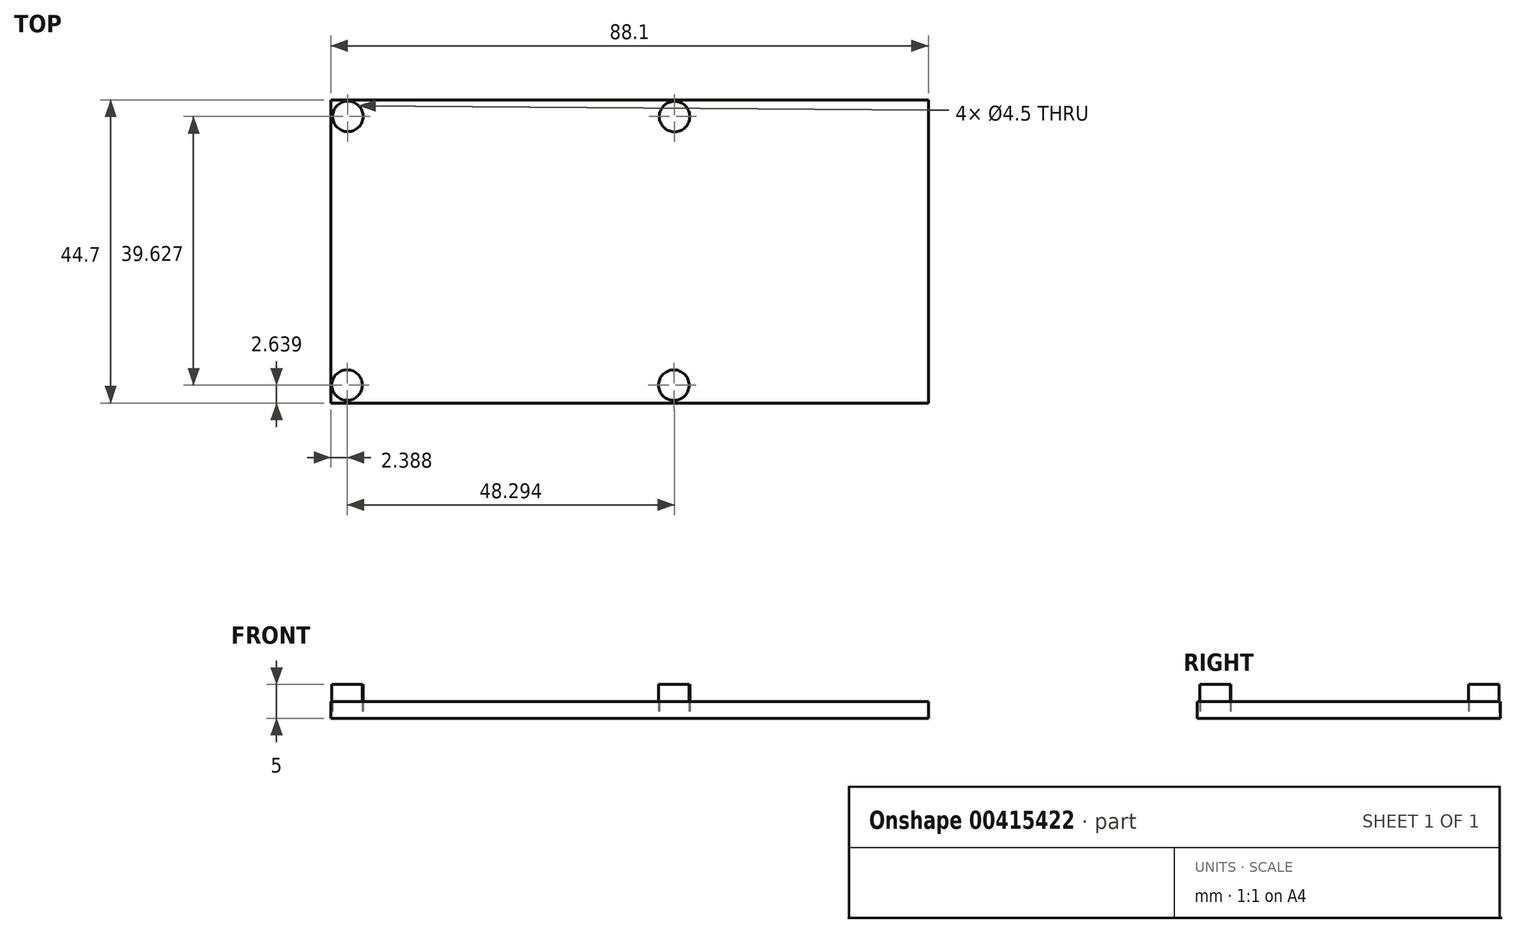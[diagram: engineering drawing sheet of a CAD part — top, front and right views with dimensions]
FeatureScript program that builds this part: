
annotation { "Feature Type Name" : "Feature", "Feature Type Description" : "" }
export const myFeature = defineFeature(function(context is Context, id is Id, definition is map)
    precondition{}
    {
        {
            var Q0;
            Q0=qCreatedBy(makeId("Top.planeOp"),FACE);
            var sketch = newSketch(context, id + "F0", { "sketchPlane" : qUnion([Q0])});
            skLineSegment(sketch, "E0.bottom", {"start": v(26.55, -22.35) * mm, "end": v(-26.55, -22.35) * mm});
            skLineSegment(sketch, "E0.top", {"start": v(26.55, 22.35) * mm, "end": v(-26.55, 22.35) * mm});
            skLineSegment(sketch, "E0.left", {"start": v(26.55, -22.35) * mm, "end": v(26.55, 22.35) * mm});
            skLineSegment(sketch, "E0.right", {"start": v(-26.55, -22.35) * mm, "end": v(-26.55, 22.35) * mm});
            skPoint(sketch, "E0.middle", {"position": v(0, 0) * mm});
            skCircle(sketch, "E1", {"center": v(-24.05, 19.92) * mm, "radius": 2.25 * mm});
            skCircle(sketch, "E2", {"center": v(24.13, 19.9) * mm, "radius": 2.25 * mm});
            skCircle(sketch, "E3", {"center": v(-24.16, -19.7) * mm, "radius": 2.25 * mm});
            skCircle(sketch, "E4", {"center": v(24.02, -19.71) * mm, "radius": 2.25 * mm});
            skSolve(sketch);
        }
        {
            var Q0;
            Q0=makeQuery(id+"F0.imprint","IMPRINT",FACE,{"disambiguationData":[TD([[makeQuery(id+"F0.imprint","IMPRINT",EDGE,{"derivedFrom":sQuery(id+"F0.wireOp",EDGE,"E2")}),1.0]])]});
            var Q1;
            Q1=makeQuery(id+"F0.imprint","IMPRINT",FACE,{"disambiguationData":[TD([[makeQuery(id+"F0.imprint","IMPRINT",EDGE,{"derivedFrom":sQuery(id+"F0.wireOp",EDGE,"E1")}),1.0]])]});
            var Q2;
            Q2=makeQuery(id+"F0.imprint","IMPRINT",FACE,{"disambiguationData":[TD([[makeQuery(id+"F0.imprint","IMPRINT",EDGE,{"derivedFrom":sQuery(id+"F0.wireOp",EDGE,"E3")}),1.0]])]});
            var Q3;
            Q3=makeQuery(id+"F0.imprint","IMPRINT",FACE,{"disambiguationData":[TD([[makeQuery(id+"F0.imprint","IMPRINT",EDGE,{"derivedFrom":sQuery(id+"F0.wireOp",EDGE,"E4")}),1.0]])]});
            extrude(context, id + "F1", {"entities" : qUnion([Q0, Q1, Q2, Q3]), "depth" : 5 * mm});
        }
        {
            var Q0;
            Q0=makeQuery(id+"F0.imprint","IMPRINT",FACE,{"disambiguationData":[TD([[makeQuery(id+"F0.imprint","IMPRINT",EDGE,{"derivedFrom":sQuery(id+"F0.wireOp",EDGE,"E0.bottom")}),-1.0]])]});
            extrude(context, id + "F2", {"entities" : qUnion([Q0]), "depth" : 2.5 * mm});
        }
        {
            var Q0;
            Q0=makeQuery(id+"F1.opExtrude","CAP_FACE",FACE,{"disambiguationData":[OSD([sQuery(id+"F0.wireOp",EDGE,"E1")])],"isStart":false});
            var sketch = newSketch(context, id + "F3", { "sketchPlane" : qUnion([Q0])});
            skSolve(sketch);
        }
        {
            var Q0;
            Q0=makeQuery(id+"F3.imprint","IMPRINT",FACE,{"disambiguationData":[TD([[makeQuery(id+"F3.imprint","IMPRINT",EDGE,{"derivedFrom":makeQuery(id+"F1.opExtrude","CAP_EDGE",EDGE,{"disambiguationData":[OSD([sQuery(id+"F0.wireOp",EDGE,"E1")])],"isStart":false})}),1.0]])]});
            var sketch = newSketch(context, id + "F4", { "sketchPlane" : qUnion([Q0])});
            skCircle(sketch, "E5", {"center": v(-24.05, 19.95) * mm, "radius": 1.25 * mm});
            skCircle(sketch, "E6", {"center": v(-24.18, -19.73) * mm, "radius": 1.25 * mm});
            skCircle(sketch, "E7", {"center": v(24.02, -19.72) * mm, "radius": 1.25 * mm});
            skCircle(sketch, "E8", {"center": v(24.14, 19.9) * mm, "radius": 1.25 * mm});
            skSolve(sketch);
        }
        {
            var Q0;
            Q0=sQuery(id+"F4.wireOp",EDGE,"E6");
            var Q1;
            Q1=sQuery(id+"F4.wireOp",EDGE,"E5");
            var Q2;
            Q2=sQuery(id+"F4.wireOp",EDGE,"E8");
            var Q3;
            Q3=sQuery(id+"F4.wireOp",EDGE,"E7");
            extrude(context, id + "F5", {"bodyType" : ToolBodyType.SURFACE, "surfaceEntities" : qUnion([Q0, Q1, Q2, Q3]), "depth" : 3 * mm});
        }
        {
            var Q0;
            Q0=makeQuery(id+"F2.opExtrude","SWEPT_FACE",FACE,{"disambiguationData":[OSD([sQuery(id+"F0.wireOp",EDGE,"E0.left")])]});
            extrude(context, id + "F6", {"entities" : qUnion([Q0]), "operationType" : NewBodyOperationType.ADD, "depth" : 35 * mm});
        }
    });
